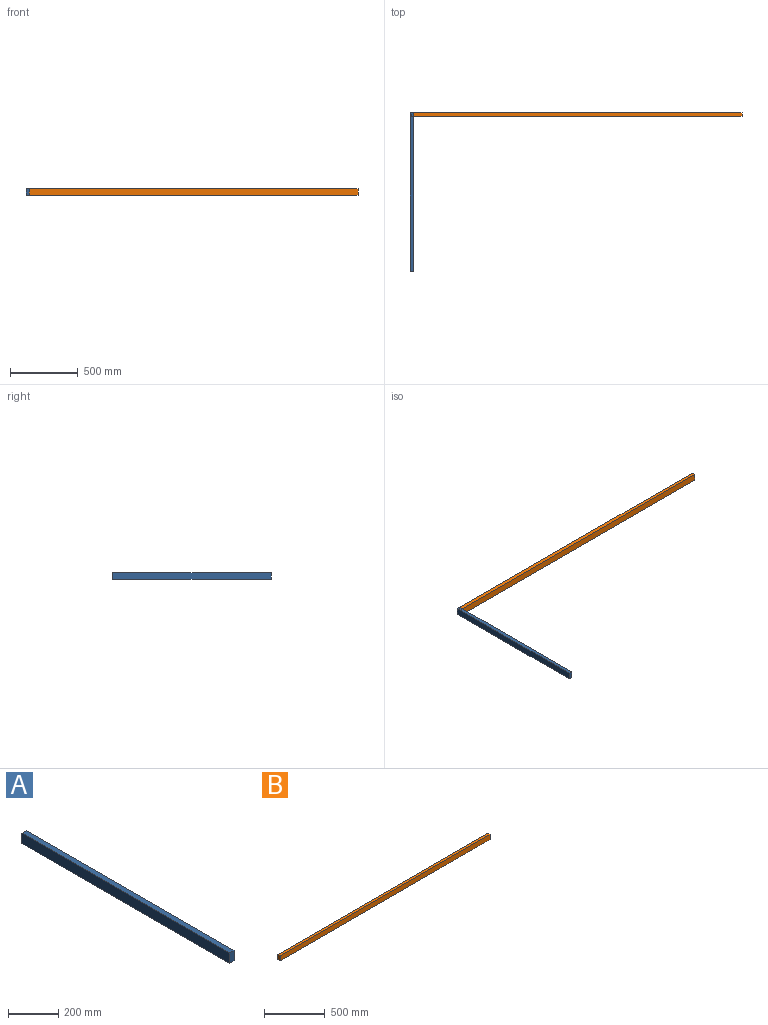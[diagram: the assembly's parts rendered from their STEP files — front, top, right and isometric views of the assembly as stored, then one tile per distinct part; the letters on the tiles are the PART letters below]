
ASSEMBLY  parts=2 mates=1
PART A: 6 faces, bbox 25.4x1168.4x50.8 mm
  f0: plane 1168.4x25.4mm, normal (0,0,-1), area 29677.4mm2, adj f1,f3,f4,f5
  f1: plane 50.8x25.4mm, normal (0,1,0), area 1290.3mm2, adj f0,f2,f4,f5
  f2: plane 1168.4x25.4mm, normal (0,0,1), area 29677.4mm2, adj f1,f3,f4,f5
  f3: plane 50.8x25.4mm, normal (0,-1,0), area 1290.3mm2, adj f0,f2,f4,f5
  f4: plane 1168.4x50.8mm, normal (1,0,0), area 59354.7mm2, adj f0,f1,f2,f3
  f5: plane 1168.4x50.8mm, normal (-1,0,0), area 59354.7mm2, adj f0,f1,f2,f3
PART B: 6 faces, bbox 2438.4x25.4x50.8 mm
  f0: plane 2438.4x25.4mm, normal (0,0,1), area 61935.4mm2, adj f1,f3,f4,f5
  f1: plane 50.8x25.4mm, normal (-1,0,0), area 1290.3mm2, adj f0,f2,f4,f5
  f2: plane 2438.4x25.4mm, normal (0,0,-1), area 61935.4mm2, adj f1,f3,f4,f5
  f3: plane 50.8x25.4mm, normal (1,0,0), area 1290.3mm2, adj f0,f2,f4,f5
  f4: plane 2438.4x50.8mm, normal (0,-1,0), area 123870.7mm2, adj f0,f1,f2,f3
  f5: plane 2438.4x50.8mm, normal (0,1,0), area 123870.7mm2, adj f0,f1,f2,f3
PLACE A rot(axis=(1,0,0),180deg) t=(-1474.8,-33.95,266.32)mm
PLACE B t=(-242.9,12.7,251.11)mm
MATE fastened A.f3 <-> B.f5  axis (0,1,0) through (-1462.1,12.7,251.11)mm
